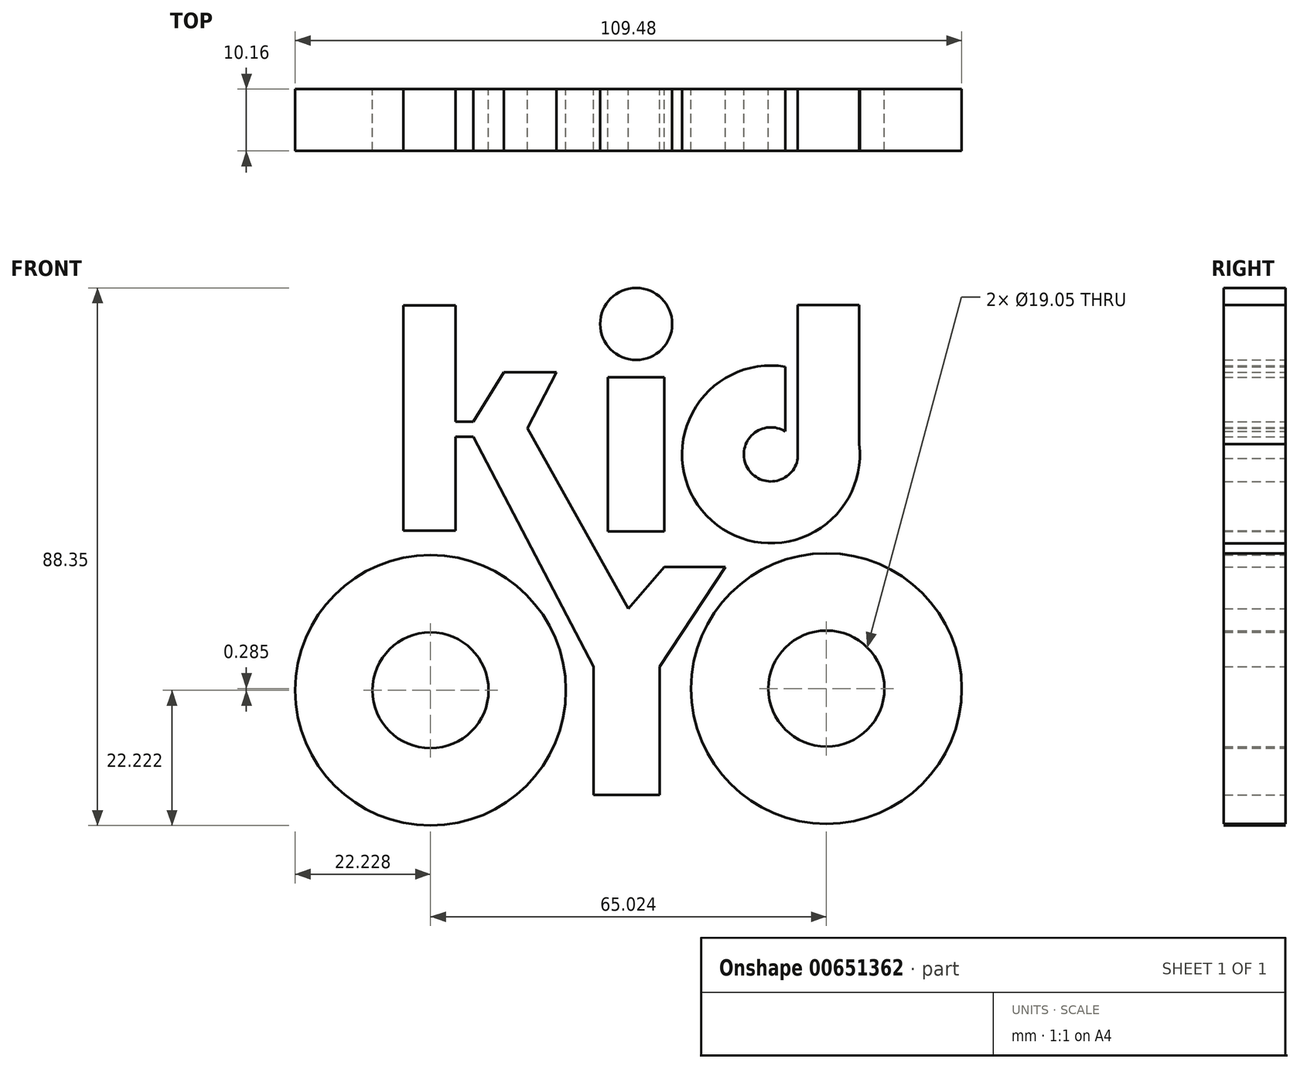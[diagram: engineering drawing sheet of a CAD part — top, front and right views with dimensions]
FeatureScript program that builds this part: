
annotation { "Feature Type Name" : "Feature", "Feature Type Description" : "" }
export const myFeature = defineFeature(function(context is Context, id is Id, definition is map)
    precondition{}
    {
        {
            var Q0;
            Q0=qCreatedBy(makeId("Front.planeOp"),FACE);
            var sketch = newSketch(context, id + "F0", { "sketchPlane" : qUnion([Q0])});
            skCircle(sketch, "E0", {"center": v(-32.51, 1.9) * mm, "radius": 22.23 * mm});
            skCircle(sketch, "E1", {"center": v(32.51, 2.19) * mm, "radius": 22.23 * mm});
            skCircle(sketch, "E2", {"center": v(-32.51, 1.9) * mm, "radius": 9.53 * mm});
            skCircle(sketch, "E3", {"center": v(32.51, 2.19) * mm, "radius": 9.53 * mm});
            skLineSegment(sketch, "E4.bottom", {"start": v(-5.72, -15.28) * mm, "end": v(5.12, -15.28) * mm});
            skLineSegment(sketch, "E4.left", {"start": v(-5.72, -15.28) * mm, "end": v(-5.72, 5.82) * mm});
            skLineSegment(sketch, "E4.right", {"start": v(5.12, -15.28) * mm, "end": v(5.12, 5.82) * mm});
            skLineSegment(sketch, "E5", {"start": v(5.12, 5.82) * mm, "end": v(15.9, 22.15) * mm});
            skLineSegment(sketch, "E6", {"start": v(15.9, 22.15) * mm, "end": v(5.91, 22.15) * mm});
            skLineSegment(sketch, "E7", {"start": v(5.91, 22.15) * mm, "end": v(0, 15.28) * mm});
            skLineSegment(sketch, "E8", {"start": v(0, 15.28) * mm, "end": v(-16.6, 44.97) * mm});
            skLineSegment(sketch, "E9", {"start": v(-16.6, 44.97) * mm, "end": v(-11.86, 54.17) * mm});
            skLineSegment(sketch, "E10", {"start": v(-11.86, 54.17) * mm, "end": v(-20.45, 54.17) * mm});
            skLineSegment(sketch, "E11", {"start": v(-20.45, 54.17) * mm, "end": v(-25.52, 46.05) * mm});
            skLineSegment(sketch, "E12", {"start": v(-25.52, 46.05) * mm, "end": v(-28.44, 46.05) * mm});
            skLineSegment(sketch, "E13.bottom", {"start": v(-36.94, 28.14) * mm, "end": v(-28.44, 28.14) * mm});
            skLineSegment(sketch, "E13.top", {"start": v(-36.94, 65.15) * mm, "end": v(-28.44, 65.15) * mm});
            skLineSegment(sketch, "E13.left", {"start": v(-36.94, 28.14) * mm, "end": v(-36.94, 65.15) * mm});
            skLineSegment(sketch, "E13.right", {"start": v(-28.44, 28.14) * mm, "end": v(-28.44, 43.6) * mm});
            skLineSegment(sketch, "E14.bottom", {"start": v(-3.39, 28.03) * mm, "end": v(5.91, 28.03) * mm});
            skLineSegment(sketch, "E14.top", {"start": v(-3.39, 53.37) * mm, "end": v(5.91, 53.37) * mm});
            skLineSegment(sketch, "E14.left", {"start": v(-3.39, 28.03) * mm, "end": v(-3.39, 53.37) * mm});
            skLineSegment(sketch, "E14.right", {"start": v(5.91, 28.03) * mm, "end": v(5.91, 53.37) * mm});
            skArc(sketch, "E15", {"start": v(25.77, 44.44) * mm, "mid": v(19.37, 38.81) * mm, "end": v(27.8, 40.04) * mm});
            skLineSegment(sketch, "E16.left", {"start": v(37.91, 65.21) * mm, "end": v(37.91, 39.39) * mm});
            skArc(sketch, "E17.trimOffspring", {"start": v(25.77, 55.09) * mm, "mid": v(12.83, 30.6) * mm, "end": v(37.91, 42.34) * mm});
            skLineSegment(sketch, "E18", {"start": v(25.77, 44.44) * mm, "end": v(25.77, 55.09) * mm});
            skLineSegment(sketch, "E19", {"start": v(27.8, 40.04) * mm, "end": v(27.8, 65.21) * mm});
            skLineSegment(sketch, "E20", {"start": v(27.8, 65.21) * mm, "end": v(37.91, 65.21) * mm});
            skCircle(sketch, "E21", {"center": v(1.27, 62.1) * mm, "radius": 5.92 * mm});
            skLineSegment(sketch, "E22", {"start": v(-28.44, 43.6) * mm, "end": v(-25.52, 43.6) * mm});
            skLineSegment(sketch, "E23", {"start": v(-25.52, 43.6) * mm, "end": v(-5.72, 5.82) * mm});
            skLineSegment(sketch, "E24.trimOffspring", {"start": v(-28.44, 46.05) * mm, "end": v(-28.44, 65.15) * mm});
            skSolve(sketch);
        }
        {
            var Q0;
            Q0 = qSketchRegion(id + "F0", true);
            extrude(context, id + "F1", {"entities" : qUnion([Q0]), "depth" : 10.16 * mm, "offsetDistance" : 25.4 * mm});
        }
    });
